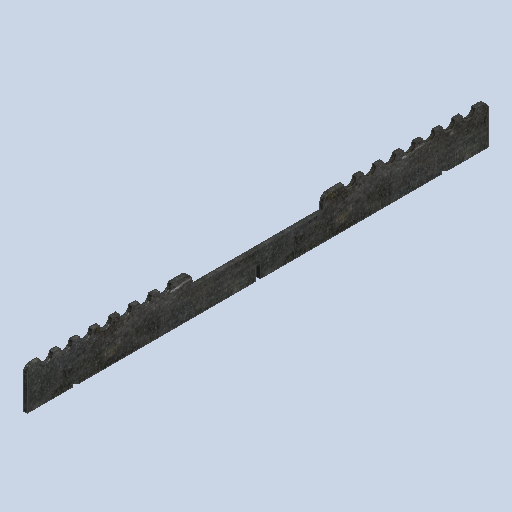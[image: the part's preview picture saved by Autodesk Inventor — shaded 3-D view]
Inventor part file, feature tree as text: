
AUTODESK INVENTOR PART (.ipt)
format: ipt  version: 2024.3 (Build 283343000, 343)  size: 362,496 bytes
history: native  units: mm
features: extrude x4, sketch x4, projected_geometry x3, fillet x2, mirror x1
ambient origin geometry x8: Origin, YZ Plane, XZ Plane, XY Plane, X Axis, Y Axis, Z Axis, Center Point
bodies: Solid1 (feature_tree)
feature tree (14):
  extrude  "Extrusion1"  Depth=350.0mm
  extrude  "Extrusion2"  Depth=100.0mm
  extrude  "Extrusion3"  Depth=10.0mm
  fillet  "Fillet1"  Radius=3.0mm
  fillet  "Fillet2"  Radius=3.1mm
  mirror  "Mirror1"
  extrude  "Extrusion5"  Depth=3.0mm TaperAngle=0.0deg
  sketch  "Sketch1"  dims[d0=30.0mm d1=350.0mm]
  sketch  "Sketch2"  dims[d2=0.0mm d3=100.0mm]
  projected_geometry  "Projected Loop1"
  sketch  "Sketch3"  dims[d4=0.0mm d5=10.0mm d6=3.0mm d7=0.0mm d8=3.1mm]
  sketch  "Sketch6"  dims[d9=20.0mm d10=3.0mm d11=0.0mm d12=10.0mm d13=10.0mm d14=10.0mm d16=10.0mm d17=10.0mm d18=10.0mm d19=15.0mm d20=15.0mm d21=15.0mm d22=15.0mm d23=15.0mm d24=15.0mm d25=10.0mm d26=15.0mm d27=3.0mm d28=0.0mm d29=5.0mm d30=5.0mm d42=45.0deg d43=3.0mm d44=3.0mm d45=195.0mm d47=2.0mm d48=0.0mm d50=97.5mm]
  projected_geometry  "Projected Loop7"
  projected_geometry  "Projected Loop8"
